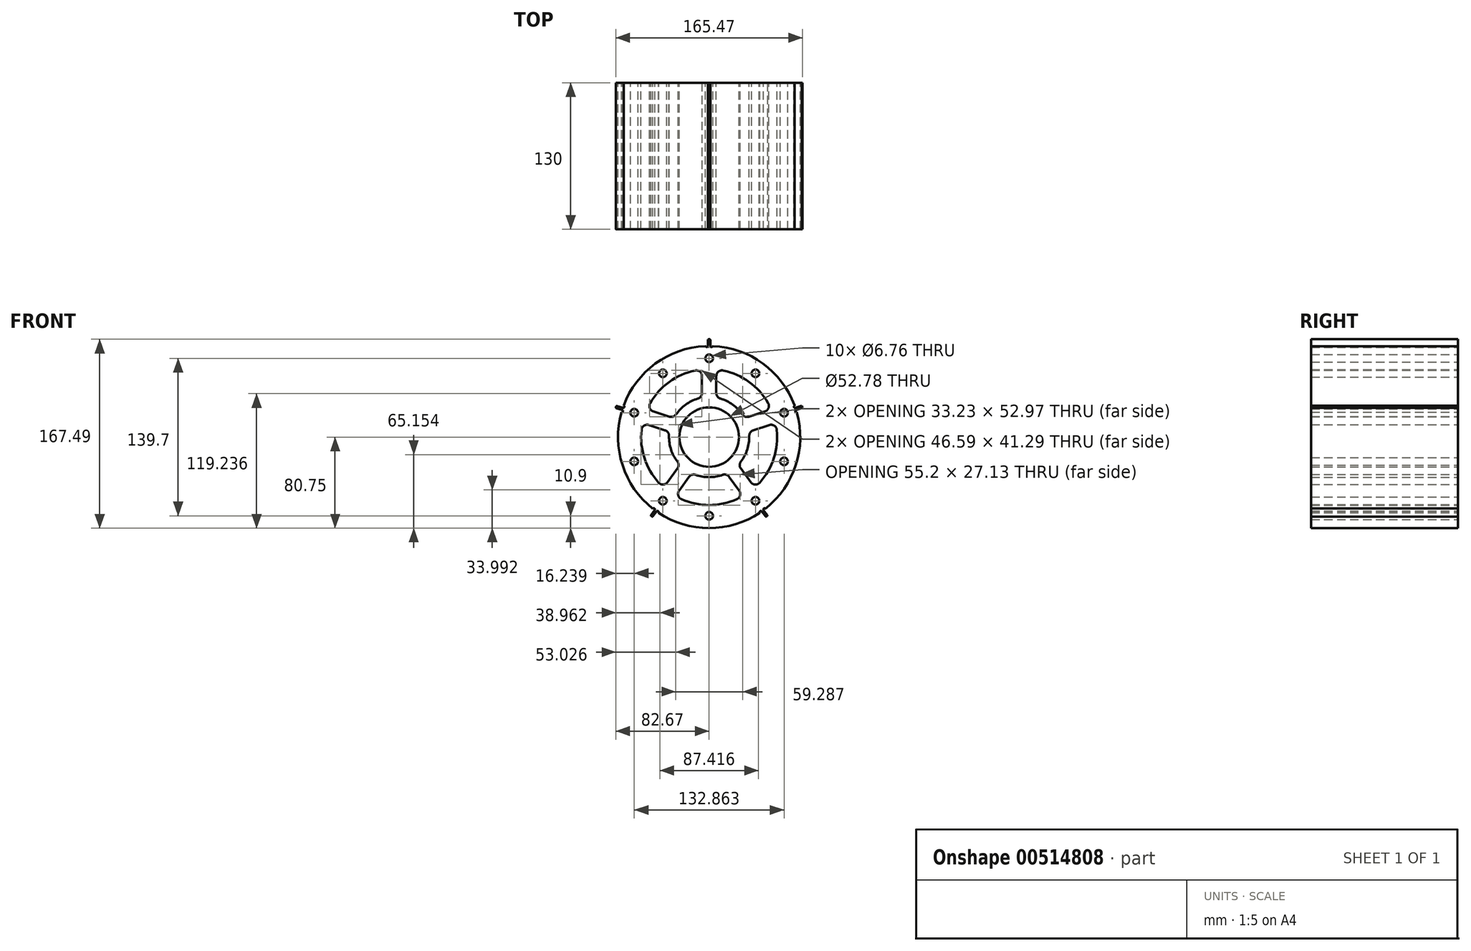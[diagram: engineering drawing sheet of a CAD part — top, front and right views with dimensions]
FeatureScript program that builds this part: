
annotation { "Feature Type Name" : "Feature", "Feature Type Description" : "" }
export const myFeature = defineFeature(function(context is Context, id is Id, definition is map)
    precondition{}
    {
        {
            var Q0;
            Q0=qCreatedBy(makeId("Front.planeOp"),FACE);
            var sketch = newSketch(context, id + "F0", { "sketchPlane" : qUnion([Q0])});
            skArc(sketch, "E0", {"start": v(-1, 80.74) * mm, "mid": v(-47.46, 65.33) * mm, "end": v(-76.48, 25.9) * mm});
            skLineSegment(sketch, "E1", {"start": v(0, 0) * mm, "end": v(0, 93.04) * mm, "construction": true});
            skLineSegment(sketch, "E2", {"start": v(-1, 86.74) * mm, "end": v(-1, 80.74) * mm});
            skLineSegment(sketch, "E3.MirrorCS", {"start": v(1, 86.74) * mm, "end": v(1, 80.74) * mm});
            skLineSegment(sketch, "E4", {"start": v(-1, 86.74) * mm, "end": v(1, 86.74) * mm});
            skLineSegment(sketch, "E5.1.0", {"start": v(-82.18, 27.75) * mm, "end": v(-76.48, 25.9) * mm});
            skLineSegment(sketch, "E5.1.1", {"start": v(-82.8, 25.85) * mm, "end": v(-82.18, 27.75) * mm});
            skLineSegment(sketch, "E5.1.2", {"start": v(-82.8, 25.85) * mm, "end": v(-77.1, 24) * mm});
            skLineSegment(sketch, "E5.2.0", {"start": v(-51.8, -69.58) * mm, "end": v(-48.27, -64.73) * mm});
            skLineSegment(sketch, "E5.2.1", {"start": v(-50.17, -70.76) * mm, "end": v(-51.8, -69.58) * mm});
            skLineSegment(sketch, "E5.2.2", {"start": v(-50.17, -70.76) * mm, "end": v(-46.65, -65.91) * mm});
            skLineSegment(sketch, "E5.3.0", {"start": v(50.17, -70.76) * mm, "end": v(46.65, -65.91) * mm});
            skLineSegment(sketch, "E5.3.1", {"start": v(51.8, -69.58) * mm, "end": v(50.17, -70.76) * mm});
            skLineSegment(sketch, "E5.3.2", {"start": v(51.8, -69.58) * mm, "end": v(48.27, -64.73) * mm});
            skArc(sketch, "E6.trimOffspring", {"start": v(-77.1, 24) * mm, "mid": v(-76.8, -24.95) * mm, "end": v(-48.27, -64.73) * mm});
            skArc(sketch, "E7.trimOffspring", {"start": v(76.48, 25.9) * mm, "mid": v(47.46, 65.33) * mm, "end": v(1, 80.74) * mm});
            skArc(sketch, "E8.trimOffspring", {"start": v(-46.65, -65.91) * mm, "mid": v(47.46, -65.33) * mm, "end": v(77.1, 24) * mm});
            skLineSegment(sketch, "E9.2.4.0", {"start": v(82.8, 25.85) * mm, "end": v(77.1, 24) * mm});
            skLineSegment(sketch, "E9.3.4.0", {"start": v(82.18, 27.75) * mm, "end": v(82.8, 25.85) * mm});
            skLineSegment(sketch, "E9.6.4.0", {"start": v(82.18, 27.75) * mm, "end": v(76.48, 25.9) * mm});
            skSolve(sketch);
        }
        {
            var Q0;
            Q0=qSketchRegion(id+"F0",true);
            extrude(context, id + "F1", {"entities" : qUnion([Q0]), "depth" : 130 * mm});
        }
        {
            var Q0;
            Q0=qCreatedBy(makeId("Front.planeOp"),FACE);
            var sketch = newSketch(context, id + "F2", { "sketchPlane" : qUnion([Q0])});
            skCircle(sketch, "E10", {"center": v(0, 0) * mm, "radius": 26.4 * mm});
            skSolve(sketch);
        }
        {
            var Q0;
            Q0=makeQuery(id+"F2.imprint","IMPRINT",FACE,{"disambiguationData":[TD([[makeQuery(id+"F2.imprint","IMPRINT",EDGE,{"derivedFrom":sQuery(id+"F2.wireOp",EDGE,"E10")}),1.0]])]});
            var Q1;
            Q1=makeQuery(id+"F1.opExtrude","CAP_FACE",FACE,{"disambiguationData":[OSD([sQuery(id+"F0.wireOp",EDGE,"E0"),sQuery(id+"F0.wireOp",EDGE,"E2"),sQuery(id+"F0.wireOp",EDGE,"E3.MirrorCS"),sQuery(id+"F0.wireOp",EDGE,"E4"),sQuery(id+"F0.wireOp",EDGE,"E5.1.0"),sQuery(id+"F0.wireOp",EDGE,"E5.1.1"),sQuery(id+"F0.wireOp",EDGE,"E5.1.2"),sQuery(id+"F0.wireOp",EDGE,"E5.2.0"),sQuery(id+"F0.wireOp",EDGE,"E5.2.1"),sQuery(id+"F0.wireOp",EDGE,"E5.2.2"),sQuery(id+"F0.wireOp",EDGE,"E5.3.0"),sQuery(id+"F0.wireOp",EDGE,"E5.3.1"),sQuery(id+"F0.wireOp",EDGE,"E5.3.2"),sQuery(id+"F0.wireOp",EDGE,"E6.trimOffspring"),sQuery(id+"F0.wireOp",EDGE,"E7.trimOffspring"),sQuery(id+"F0.wireOp",EDGE,"E8.trimOffspring")])],"isStart":false});
            extrude(context, id + "F3", {"entities" : qUnion([Q0]), "operationType" : NewBodyOperationType.REMOVE, "endBound" : BoundingType.UP_TO_SURFACE, "endBoundEntityFace" : qUnion([Q1]), "depth" : 25.4 * mm});
        }
        {
            var Q0;
            Q0=qCreatedBy(makeId("Front.planeOp"),FACE);
            var sketch = newSketch(context, id + "F4", { "sketchPlane" : qUnion([Q0])});
            skLineSegment(sketch, "E11", {"start": v(9.9, 57.53) * mm, "end": v(9.9, 40.92) * mm});
            skLineSegment(sketch, "E12", {"start": v(40.92, 9.9) * mm, "end": v(57.53, 9.9) * mm});
            skArc(sketch, "E13", {"start": v(66.9, 23.04) * mm, "mid": v(50.03, 50.03) * mm, "end": v(23.04, 66.9) * mm});
            skArc(sketch, "E14", {"start": v(32, 15.5) * mm, "mid": v(25.14, 25.14) * mm, "end": v(15.5, 32) * mm});
            skArc(sketch, "E15.filletArc", {"start": v(32, 15.5) * mm, "mid": v(35.66, 11.42) * mm, "end": v(40.92, 9.9) * mm});
            skArc(sketch, "E16.filletArc", {"start": v(9.9, 40.92) * mm, "mid": v(11.42, 35.66) * mm, "end": v(15.5, 32) * mm});
            skArc(sketch, "E17.filletArc", {"start": v(23.04, 66.9) * mm, "mid": v(14.06, 65.6) * mm, "end": v(9.9, 57.53) * mm});
            skArc(sketch, "E18.filletArc", {"start": v(57.53, 9.9) * mm, "mid": v(65.6, 14.06) * mm, "end": v(66.9, 23.04) * mm});
            skLineSegment(sketch, "E19", {"start": v(0, 0) * mm, "end": v(0, 68.56) * mm, "construction": true});
            skLineSegment(sketch, "E20", {"start": v(0, 0) * mm, "end": v(60.99, 0) * mm, "construction": true});
            skLineSegment(sketch, "E21.1.0", {"start": v(-57.53, 9.9) * mm, "end": v(-40.92, 9.9) * mm});
            skArc(sketch, "E21.1.1", {"start": v(-66.9, 23.04) * mm, "mid": v(-65.6, 14.06) * mm, "end": v(-57.53, 9.9) * mm});
            skArc(sketch, "E21.1.2", {"start": v(-23.04, 66.9) * mm, "mid": v(-50.03, 50.03) * mm, "end": v(-66.9, 23.04) * mm});
            skArc(sketch, "E21.1.3", {"start": v(-9.9, 57.53) * mm, "mid": v(-14.06, 65.6) * mm, "end": v(-23.04, 66.9) * mm});
            skLineSegment(sketch, "E21.1.4", {"start": v(-9.9, 40.92) * mm, "end": v(-9.9, 57.53) * mm});
            skArc(sketch, "E21.1.5", {"start": v(-15.5, 32) * mm, "mid": v(-11.42, 35.66) * mm, "end": v(-9.9, 40.92) * mm});
            skArc(sketch, "E21.1.6", {"start": v(-40.92, 9.9) * mm, "mid": v(-35.66, 11.42) * mm, "end": v(-32, 15.5) * mm});
            skArc(sketch, "E21.1.7", {"start": v(-15.5, 32) * mm, "mid": v(-25.14, 25.14) * mm, "end": v(-32, 15.5) * mm});
            skLineSegment(sketch, "E21.2.0", {"start": v(-9.9, -57.53) * mm, "end": v(-9.9, -40.92) * mm});
            skArc(sketch, "E21.2.1", {"start": v(-23.04, -66.9) * mm, "mid": v(-14.06, -65.6) * mm, "end": v(-9.9, -57.53) * mm});
            skArc(sketch, "E21.2.2", {"start": v(-66.9, -23.04) * mm, "mid": v(-50.03, -50.03) * mm, "end": v(-23.04, -66.9) * mm});
            skArc(sketch, "E21.2.3", {"start": v(-57.53, -9.9) * mm, "mid": v(-65.6, -14.06) * mm, "end": v(-66.9, -23.04) * mm});
            skLineSegment(sketch, "E21.2.4", {"start": v(-40.92, -9.9) * mm, "end": v(-57.53, -9.9) * mm});
            skArc(sketch, "E21.2.5", {"start": v(-32, -15.5) * mm, "mid": v(-35.66, -11.42) * mm, "end": v(-40.92, -9.9) * mm});
            skArc(sketch, "E21.2.6", {"start": v(-9.9, -40.92) * mm, "mid": v(-11.42, -35.66) * mm, "end": v(-15.5, -32) * mm});
            skArc(sketch, "E21.2.7", {"start": v(-32, -15.5) * mm, "mid": v(-25.14, -25.14) * mm, "end": v(-15.5, -32) * mm});
            skLineSegment(sketch, "E21.3.0", {"start": v(57.53, -9.9) * mm, "end": v(40.92, -9.9) * mm});
            skArc(sketch, "E21.3.1", {"start": v(66.9, -23.04) * mm, "mid": v(65.6, -14.06) * mm, "end": v(57.53, -9.9) * mm});
            skArc(sketch, "E21.3.2", {"start": v(23.04, -66.9) * mm, "mid": v(50.03, -50.03) * mm, "end": v(66.9, -23.04) * mm});
            skArc(sketch, "E21.3.3", {"start": v(9.9, -57.53) * mm, "mid": v(14.06, -65.6) * mm, "end": v(23.04, -66.9) * mm});
            skLineSegment(sketch, "E21.3.4", {"start": v(9.9, -40.92) * mm, "end": v(9.9, -57.53) * mm});
            skArc(sketch, "E21.3.5", {"start": v(15.5, -32) * mm, "mid": v(11.42, -35.66) * mm, "end": v(9.9, -40.92) * mm});
            skArc(sketch, "E21.3.6", {"start": v(40.92, -9.9) * mm, "mid": v(35.66, -11.42) * mm, "end": v(32, -15.5) * mm});
            skArc(sketch, "E21.3.7", {"start": v(15.5, -32) * mm, "mid": v(25.14, -25.14) * mm, "end": v(32, -15.5) * mm});
            skSolve(sketch);
        }
        {
            var Q0;
            Q0=makeQuery(id+"F1.opExtrude","CAP_FACE",FACE,{"disambiguationData":[OSD([sQuery(id+"F0.wireOp",EDGE,"E0"),sQuery(id+"F0.wireOp",EDGE,"E2"),sQuery(id+"F0.wireOp",EDGE,"E3.MirrorCS"),sQuery(id+"F0.wireOp",EDGE,"E4"),sQuery(id+"F0.wireOp",EDGE,"E5.1.0"),sQuery(id+"F0.wireOp",EDGE,"E5.1.1"),sQuery(id+"F0.wireOp",EDGE,"E5.1.2"),sQuery(id+"F0.wireOp",EDGE,"E5.2.0"),sQuery(id+"F0.wireOp",EDGE,"E5.2.1"),sQuery(id+"F0.wireOp",EDGE,"E5.2.2"),sQuery(id+"F0.wireOp",EDGE,"E5.3.0"),sQuery(id+"F0.wireOp",EDGE,"E5.3.1"),sQuery(id+"F0.wireOp",EDGE,"E5.3.2"),sQuery(id+"F0.wireOp",EDGE,"E6.trimOffspring"),sQuery(id+"F0.wireOp",EDGE,"E7.trimOffspring"),sQuery(id+"F0.wireOp",EDGE,"E8.trimOffspring")])],"isStart":true});
            var sketch = newSketch(context, id + "F5", { "sketchPlane" : qUnion([Q0])});
            skLineSegment(sketch, "E22", {"start": v(-1, 80.74) * mm, "end": v(-7.67, 80.74) * mm, "construction": true});
            skCircle(sketch, "E23", {"center": v(-2.02, 80.74) * mm, "radius": 1.02 * mm});
            skCircle(sketch, "E24.MirrorC", {"center": v(2.02, 80.74) * mm, "radius": 1.02 * mm});
            skCircle(sketch, "E25.1.0", {"center": v(-76.17, 26.87) * mm, "radius": 1.02 * mm});
            skCircle(sketch, "E25.1.1", {"center": v(-77.41, 23.03) * mm, "radius": 1.02 * mm});
            skCircle(sketch, "E25.2.0", {"center": v(-49.1, -64.14) * mm, "radius": 1.02 * mm});
            skCircle(sketch, "E25.2.1", {"center": v(-45.83, -66.5) * mm, "radius": 1.02 * mm});
            skCircle(sketch, "E25.3.0", {"center": v(45.83, -66.5) * mm, "radius": 1.02 * mm});
            skCircle(sketch, "E25.3.1", {"center": v(49.1, -64.14) * mm, "radius": 1.02 * mm});
            skPoint(sketch, "E25.center", {"position": v(0, 0) * mm});
            skCircle(sketch, "E26.1.4.0", {"center": v(77.41, 23.03) * mm, "radius": 1.02 * mm});
            skCircle(sketch, "E26.2.4.0", {"center": v(76.17, 26.87) * mm, "radius": 1.02 * mm});
            skSolve(sketch);
        }
        {
            var Q0;
            Q0=qSketchRegion(id+"F5",true);
            extrude(context, id + "F6", {"entities" : qUnion([Q0]), "operationType" : NewBodyOperationType.REMOVE, "endBound" : BoundingType.THROUGH_ALL, "oppositeDirection" : true, "depth" : 25.4 * mm});
        }
        {
            var Q0;
            Q0=makeQuery(id+"F1.opExtrude","SWEPT_EDGE",EDGE,{"disambiguationData":[OSD([sQuery(id+"F0.wireOp",EDGE,"E2"),sQuery(id+"F0.wireOp",EDGE,"E4")])]});
            var Q1;
            Q1=makeQuery(id+"F1.opExtrude","SWEPT_EDGE",EDGE,{"disambiguationData":[OSD([sQuery(id+"F0.wireOp",EDGE,"E3.MirrorCS"),sQuery(id+"F0.wireOp",EDGE,"E4")])]});
            var Q2;
            Q2=makeQuery(id+"F6.boolean.opBoolean","INTERSECT",EDGE,{"derivedFrom":[makeQuery(id+"F1.opExtrude","SWEPT_FACE",FACE,{"disambiguationData":[OSD([sQuery(id+"F0.wireOp",EDGE,"E0")])]}),makeQuery(id+"F6.opExtrude","SWEPT_FACE",FACE,{"disambiguationData":[OSD([sQuery(id+"F5.wireOp",EDGE,"E24.MirrorC")])]})]});
            var Q3;
            Q3=makeQuery(id+"F6.boolean.opBoolean","INTERSECT",EDGE,{"derivedFrom":[makeQuery(id+"F1.opExtrude","SWEPT_FACE",FACE,{"disambiguationData":[OSD([sQuery(id+"F0.wireOp",EDGE,"E7.trimOffspring")])]}),makeQuery(id+"F6.opExtrude","SWEPT_FACE",FACE,{"disambiguationData":[OSD([sQuery(id+"F5.wireOp",EDGE,"E23")])]})]});
            var Q4;
            Q4=makeQuery(id+"F6.boolean.opBoolean","INTERSECT",EDGE,{"derivedFrom":[makeQuery(id+"F1.opExtrude","SWEPT_FACE",FACE,{"disambiguationData":[OSD([sQuery(id+"F0.wireOp",EDGE,"E0")])]}),makeQuery(id+"F6.opExtrude","SWEPT_FACE",FACE,{"disambiguationData":[OSD([sQuery(id+"F5.wireOp",EDGE,"E25.3.1")])]})]});
            var Q5;
            Q5=makeQuery(id+"F1.opExtrude","SWEPT_EDGE",EDGE,{"disambiguationData":[OSD([sQuery(id+"F0.wireOp",EDGE,"E5.1.0"),sQuery(id+"F0.wireOp",EDGE,"E5.1.1")])]});
            var Q6;
            Q6=makeQuery(id+"F1.opExtrude","SWEPT_EDGE",EDGE,{"disambiguationData":[OSD([sQuery(id+"F0.wireOp",EDGE,"E5.1.1"),sQuery(id+"F0.wireOp",EDGE,"E5.1.2")])]});
            var Q7;
            Q7=makeQuery(id+"F6.boolean.opBoolean","INTERSECT",EDGE,{"derivedFrom":[makeQuery(id+"F1.opExtrude","SWEPT_FACE",FACE,{"disambiguationData":[OSD([sQuery(id+"F0.wireOp",EDGE,"E6.trimOffspring")])]}),makeQuery(id+"F6.opExtrude","SWEPT_FACE",FACE,{"disambiguationData":[OSD([sQuery(id+"F5.wireOp",EDGE,"E25.3.0")])]})]});
            var Q8;
            Q8=makeQuery(id+"F6.boolean.opBoolean","INTERSECT",EDGE,{"derivedFrom":[makeQuery(id+"F1.opExtrude","SWEPT_FACE",FACE,{"disambiguationData":[OSD([sQuery(id+"F0.wireOp",EDGE,"E6.trimOffspring")])]}),makeQuery(id+"F6.opExtrude","SWEPT_FACE",FACE,{"disambiguationData":[OSD([sQuery(id+"F5.wireOp",EDGE,"E25.2.1")])]})]});
            var Q9;
            Q9=makeQuery(id+"F1.opExtrude","SWEPT_EDGE",EDGE,{"disambiguationData":[OSD([sQuery(id+"F0.wireOp",EDGE,"E5.2.0"),sQuery(id+"F0.wireOp",EDGE,"E5.2.1")])]});
            var Q10;
            Q10=makeQuery(id+"F1.opExtrude","SWEPT_EDGE",EDGE,{"disambiguationData":[OSD([sQuery(id+"F0.wireOp",EDGE,"E5.2.1"),sQuery(id+"F0.wireOp",EDGE,"E5.2.2")])]});
            var Q11;
            Q11=makeQuery(id+"F6.boolean.opBoolean","INTERSECT",EDGE,{"derivedFrom":[makeQuery(id+"F1.opExtrude","SWEPT_FACE",FACE,{"disambiguationData":[OSD([sQuery(id+"F0.wireOp",EDGE,"E8.trimOffspring")])]}),makeQuery(id+"F6.opExtrude","SWEPT_FACE",FACE,{"disambiguationData":[OSD([sQuery(id+"F5.wireOp",EDGE,"E25.2.0")])]})]});
            var Q12;
            Q12=makeQuery(id+"F6.boolean.opBoolean","INTERSECT",EDGE,{"derivedFrom":[makeQuery(id+"F1.opExtrude","SWEPT_FACE",FACE,{"disambiguationData":[OSD([sQuery(id+"F0.wireOp",EDGE,"E8.trimOffspring")])]}),makeQuery(id+"F6.opExtrude","SWEPT_FACE",FACE,{"disambiguationData":[OSD([sQuery(id+"F5.wireOp",EDGE,"E25.1.1")])]})]});
            var Q13;
            Q13=makeQuery(id+"F1.opExtrude","SWEPT_EDGE",EDGE,{"disambiguationData":[OSD([sQuery(id+"F0.wireOp",EDGE,"E5.3.0"),sQuery(id+"F0.wireOp",EDGE,"E5.3.1")])]});
            var Q14;
            Q14=makeQuery(id+"F1.opExtrude","SWEPT_EDGE",EDGE,{"disambiguationData":[OSD([sQuery(id+"F0.wireOp",EDGE,"E5.3.1"),sQuery(id+"F0.wireOp",EDGE,"E5.3.2")])]});
            var Q15;
            Q15=makeQuery(id+"F6.boolean.opBoolean","INTERSECT",EDGE,{"derivedFrom":[makeQuery(id+"F1.opExtrude","SWEPT_FACE",FACE,{"disambiguationData":[OSD([sQuery(id+"F0.wireOp",EDGE,"E7.trimOffspring")])]}),makeQuery(id+"F6.opExtrude","SWEPT_FACE",FACE,{"disambiguationData":[OSD([sQuery(id+"F5.wireOp",EDGE,"E25.1.0")])]})]});
            fillet(context, id + "F7", {"entities" : qUnion([Q0, Q1, Q2, Q3, Q4, Q5, Q6, Q7, Q8, Q9, Q10, Q11, Q12, Q13, Q14, Q15]), "radius" : 0.5 * mm, "tangentPropagation" : true, "allowEdgeOverflow" : false});
        }
        {
            var Q0;
            Q0=makeQuery(id+"F1.opExtrude","CAP_FACE",FACE,{"disambiguationData":[OSD([sQuery(id+"F0.wireOp",EDGE,"E0"),sQuery(id+"F0.wireOp",EDGE,"E2"),sQuery(id+"F0.wireOp",EDGE,"E3.MirrorCS"),sQuery(id+"F0.wireOp",EDGE,"E4"),sQuery(id+"F0.wireOp",EDGE,"E5.1.0"),sQuery(id+"F0.wireOp",EDGE,"E5.1.1"),sQuery(id+"F0.wireOp",EDGE,"E5.1.2"),sQuery(id+"F0.wireOp",EDGE,"E5.2.0"),sQuery(id+"F0.wireOp",EDGE,"E5.2.1"),sQuery(id+"F0.wireOp",EDGE,"E5.2.2"),sQuery(id+"F0.wireOp",EDGE,"E5.3.0"),sQuery(id+"F0.wireOp",EDGE,"E5.3.1"),sQuery(id+"F0.wireOp",EDGE,"E5.3.2"),sQuery(id+"F0.wireOp",EDGE,"E6.trimOffspring"),sQuery(id+"F0.wireOp",EDGE,"E7.trimOffspring"),sQuery(id+"F0.wireOp",EDGE,"E8.trimOffspring"),sQuery(id+"F0.wireOp",EDGE,"E9.2.4.0"),sQuery(id+"F0.wireOp",EDGE,"E9.3.4.0"),sQuery(id+"F0.wireOp",EDGE,"E9.6.4.0")])],"isStart":true});
            var sketch = newSketch(context, id + "F8", { "sketchPlane" : qUnion([Q0])});
            skArc(sketch, "E27", {"start": v(-6.35, 59.99) * mm, "mid": v(-35.46, 48.8) * mm, "end": v(-55.1, 24.58) * mm});
            skArc(sketch, "E28", {"start": v(-6.35, 34.99) * mm, "mid": v(-20.9, 28.77) * mm, "end": v(-31.31, 16.85) * mm});
            skLineSegment(sketch, "E29", {"start": v(-6.35, 59.99) * mm, "end": v(-6.35, 34.99) * mm});
            skLineSegment(sketch, "E30", {"start": v(6.35, 59.99) * mm, "end": v(6.35, 34.99) * mm});
            skLineSegment(sketch, "E31.1.0", {"start": v(-59.02, 12.5) * mm, "end": v(-35.24, 4.77) * mm});
            skLineSegment(sketch, "E31.1.1", {"start": v(-55.1, 24.58) * mm, "end": v(-31.31, 16.85) * mm});
            skLineSegment(sketch, "E31.2.0", {"start": v(-30.12, -52.27) * mm, "end": v(-15.43, -32.04) * mm});
            skLineSegment(sketch, "E31.2.1", {"start": v(-40.4, -44.8) * mm, "end": v(-25.7, -24.57) * mm});
            skLineSegment(sketch, "E31.3.0", {"start": v(40.4, -44.8) * mm, "end": v(25.7, -24.57) * mm});
            skLineSegment(sketch, "E31.3.1", {"start": v(30.12, -52.27) * mm, "end": v(15.43, -32.04) * mm});
            skLineSegment(sketch, "E31.4.0", {"start": v(55.1, 24.58) * mm, "end": v(31.31, 16.85) * mm});
            skLineSegment(sketch, "E31.4.1", {"start": v(59.02, 12.5) * mm, "end": v(35.24, 4.77) * mm});
            skArc(sketch, "E32.trimOffspring", {"start": v(-59.02, 12.5) * mm, "mid": v(-57.37, -18.64) * mm, "end": v(-40.4, -44.8) * mm});
            skArc(sketch, "E33.trimOffspring", {"start": v(-35.24, 4.77) * mm, "mid": v(-33.82, -10.99) * mm, "end": v(-25.7, -24.57) * mm});
            skArc(sketch, "E34.trimOffspring", {"start": v(-15.43, -32.04) * mm, "mid": v(0, -35.56) * mm, "end": v(15.43, -32.04) * mm});
            skArc(sketch, "E35.trimOffspring", {"start": v(-30.12, -52.27) * mm, "mid": v(0, -60.33) * mm, "end": v(30.12, -52.27) * mm});
            skArc(sketch, "E36.trimOffspring", {"start": v(40.4, -44.8) * mm, "mid": v(57.37, -18.64) * mm, "end": v(59.02, 12.5) * mm});
            skArc(sketch, "E37.trimOffspring", {"start": v(25.7, -24.57) * mm, "mid": v(33.82, -10.99) * mm, "end": v(35.24, 4.77) * mm});
            skArc(sketch, "E38.trimOffspring", {"start": v(31.31, 16.85) * mm, "mid": v(20.9, 28.77) * mm, "end": v(6.35, 34.99) * mm});
            skArc(sketch, "E39.trimOffspring", {"start": v(55.1, 24.58) * mm, "mid": v(35.46, 48.8) * mm, "end": v(6.35, 59.99) * mm});
            skSolve(sketch);
        }
        {
            var Q0;
            Q0=makeQuery(id+"F8.imprint","IMPRINT",FACE,{"disambiguationData":[TD([[makeQuery(id+"F8.imprint","IMPRINT",EDGE,{"derivedFrom":sQuery(id+"F8.wireOp",EDGE,"E27")}),1.0]])]});
            var Q1;
            Q1=makeQuery(id+"F8.imprint","IMPRINT",FACE,{"disambiguationData":[TD([[makeQuery(id+"F8.imprint","IMPRINT",EDGE,{"derivedFrom":sQuery(id+"F8.wireOp",EDGE,"E30")}),1.0]])]});
            var Q2;
            Q2=makeQuery(id+"F8.imprint","IMPRINT",FACE,{"disambiguationData":[TD([[makeQuery(id+"F8.imprint","IMPRINT",EDGE,{"derivedFrom":sQuery(id+"F8.wireOp",EDGE,"E31.3.0")}),-1.0]])]});
            var Q3;
            Q3=makeQuery(id+"F8.imprint","IMPRINT",FACE,{"disambiguationData":[TD([[makeQuery(id+"F8.imprint","IMPRINT",EDGE,{"derivedFrom":sQuery(id+"F8.wireOp",EDGE,"E31.2.0")}),-1.0]])]});
            var Q4;
            Q4=makeQuery(id+"F8.imprint","IMPRINT",FACE,{"disambiguationData":[TD([[makeQuery(id+"F8.imprint","IMPRINT",EDGE,{"derivedFrom":sQuery(id+"F8.wireOp",EDGE,"E31.1.0")}),-1.0]])]});
            extrude(context, id + "F9", {"entities" : qUnion([Q0, Q1, Q2, Q3, Q4]), "operationType" : NewBodyOperationType.REMOVE, "endBound" : BoundingType.THROUGH_ALL, "oppositeDirection" : true, "depth" : 25.4 * mm});
        }
        {
            var Q0;
            Q0=makeQuery(id+"F9.boolean.opBoolean","COPY",EDGE,{"derivedFrom":makeQuery(id+"F9.opExtrude","SWEPT_EDGE",EDGE,{"disambiguationData":[OSD([sQuery(id+"F8.wireOp",EDGE,"E27"),sQuery(id+"F8.wireOp",EDGE,"E31.1.1")])]})});
            var Q1;
            Q1=makeQuery(id+"F9.boolean.opBoolean","COPY",EDGE,{"derivedFrom":makeQuery(id+"F9.opExtrude","SWEPT_EDGE",EDGE,{"disambiguationData":[OSD([sQuery(id+"F8.wireOp",EDGE,"E28"),sQuery(id+"F8.wireOp",EDGE,"E31.1.1")])]})});
            var Q2;
            Q2=makeQuery(id+"F9.boolean.opBoolean","COPY",EDGE,{"derivedFrom":makeQuery(id+"F9.opExtrude","SWEPT_EDGE",EDGE,{"disambiguationData":[OSD([sQuery(id+"F8.wireOp",EDGE,"E28"),sQuery(id+"F8.wireOp",EDGE,"E29")])]})});
            var Q3;
            Q3=makeQuery(id+"F9.boolean.opBoolean","COPY",EDGE,{"derivedFrom":makeQuery(id+"F9.opExtrude","SWEPT_EDGE",EDGE,{"disambiguationData":[OSD([sQuery(id+"F8.wireOp",EDGE,"E27"),sQuery(id+"F8.wireOp",EDGE,"E29")])]})});
            var Q4;
            Q4=makeQuery(id+"F9.boolean.opBoolean","COPY",EDGE,{"derivedFrom":makeQuery(id+"F9.opExtrude","SWEPT_EDGE",EDGE,{"disambiguationData":[OSD([sQuery(id+"F8.wireOp",EDGE,"E31.4.0"),sQuery(id+"F8.wireOp",EDGE,"E39.trimOffspring")])]})});
            var Q5;
            Q5=makeQuery(id+"F9.boolean.opBoolean","COPY",EDGE,{"derivedFrom":makeQuery(id+"F9.opExtrude","SWEPT_EDGE",EDGE,{"disambiguationData":[OSD([sQuery(id+"F8.wireOp",EDGE,"E31.4.0"),sQuery(id+"F8.wireOp",EDGE,"E38.trimOffspring")])]})});
            var Q6;
            Q6=makeQuery(id+"F9.boolean.opBoolean","COPY",EDGE,{"derivedFrom":makeQuery(id+"F9.opExtrude","SWEPT_EDGE",EDGE,{"disambiguationData":[OSD([sQuery(id+"F8.wireOp",EDGE,"E30"),sQuery(id+"F8.wireOp",EDGE,"E38.trimOffspring")])]})});
            var Q7;
            Q7=makeQuery(id+"F9.boolean.opBoolean","COPY",EDGE,{"derivedFrom":makeQuery(id+"F9.opExtrude","SWEPT_EDGE",EDGE,{"disambiguationData":[OSD([sQuery(id+"F8.wireOp",EDGE,"E30"),sQuery(id+"F8.wireOp",EDGE,"E39.trimOffspring")])]})});
            var Q8;
            Q8=makeQuery(id+"F9.boolean.opBoolean","COPY",EDGE,{"derivedFrom":makeQuery(id+"F9.opExtrude","SWEPT_EDGE",EDGE,{"disambiguationData":[OSD([sQuery(id+"F8.wireOp",EDGE,"E31.4.1"),sQuery(id+"F8.wireOp",EDGE,"E36.trimOffspring")])]})});
            var Q9;
            Q9=makeQuery(id+"F9.boolean.opBoolean","COPY",EDGE,{"derivedFrom":makeQuery(id+"F9.opExtrude","SWEPT_EDGE",EDGE,{"disambiguationData":[OSD([sQuery(id+"F8.wireOp",EDGE,"E31.3.0"),sQuery(id+"F8.wireOp",EDGE,"E36.trimOffspring")])]})});
            var Q10;
            Q10=makeQuery(id+"F9.boolean.opBoolean","COPY",EDGE,{"derivedFrom":makeQuery(id+"F9.opExtrude","SWEPT_EDGE",EDGE,{"disambiguationData":[OSD([sQuery(id+"F8.wireOp",EDGE,"E31.3.0"),sQuery(id+"F8.wireOp",EDGE,"E37.trimOffspring")])]})});
            var Q11;
            Q11=makeQuery(id+"F9.boolean.opBoolean","COPY",EDGE,{"derivedFrom":makeQuery(id+"F9.opExtrude","SWEPT_EDGE",EDGE,{"disambiguationData":[OSD([sQuery(id+"F8.wireOp",EDGE,"E31.4.1"),sQuery(id+"F8.wireOp",EDGE,"E37.trimOffspring")])]})});
            var Q12;
            Q12=makeQuery(id+"F9.boolean.opBoolean","COPY",EDGE,{"derivedFrom":makeQuery(id+"F9.opExtrude","SWEPT_EDGE",EDGE,{"disambiguationData":[OSD([sQuery(id+"F8.wireOp",EDGE,"E31.2.0"),sQuery(id+"F8.wireOp",EDGE,"E35.trimOffspring")])]})});
            var Q13;
            Q13=makeQuery(id+"F9.boolean.opBoolean","COPY",EDGE,{"derivedFrom":makeQuery(id+"F9.opExtrude","SWEPT_EDGE",EDGE,{"disambiguationData":[OSD([sQuery(id+"F8.wireOp",EDGE,"E31.3.1"),sQuery(id+"F8.wireOp",EDGE,"E35.trimOffspring")])]})});
            var Q14;
            Q14=makeQuery(id+"F9.boolean.opBoolean","COPY",EDGE,{"derivedFrom":makeQuery(id+"F9.opExtrude","SWEPT_EDGE",EDGE,{"disambiguationData":[OSD([sQuery(id+"F8.wireOp",EDGE,"E31.3.1"),sQuery(id+"F8.wireOp",EDGE,"E34.trimOffspring")])]})});
            var Q15;
            Q15=makeQuery(id+"F9.boolean.opBoolean","COPY",EDGE,{"derivedFrom":makeQuery(id+"F9.opExtrude","SWEPT_EDGE",EDGE,{"disambiguationData":[OSD([sQuery(id+"F8.wireOp",EDGE,"E31.2.0"),sQuery(id+"F8.wireOp",EDGE,"E34.trimOffspring")])]})});
            var Q16;
            Q16=makeQuery(id+"F9.boolean.opBoolean","COPY",EDGE,{"derivedFrom":makeQuery(id+"F9.opExtrude","SWEPT_EDGE",EDGE,{"disambiguationData":[OSD([sQuery(id+"F8.wireOp",EDGE,"E31.1.0"),sQuery(id+"F8.wireOp",EDGE,"E33.trimOffspring")])]})});
            var Q17;
            Q17=makeQuery(id+"F9.boolean.opBoolean","COPY",EDGE,{"derivedFrom":makeQuery(id+"F9.opExtrude","SWEPT_EDGE",EDGE,{"disambiguationData":[OSD([sQuery(id+"F8.wireOp",EDGE,"E31.2.1"),sQuery(id+"F8.wireOp",EDGE,"E33.trimOffspring")])]})});
            var Q18;
            Q18=makeQuery(id+"F9.boolean.opBoolean","COPY",EDGE,{"derivedFrom":makeQuery(id+"F9.opExtrude","SWEPT_EDGE",EDGE,{"disambiguationData":[OSD([sQuery(id+"F8.wireOp",EDGE,"E31.2.1"),sQuery(id+"F8.wireOp",EDGE,"E32.trimOffspring")])]})});
            var Q19;
            Q19=makeQuery(id+"F9.boolean.opBoolean","COPY",EDGE,{"derivedFrom":makeQuery(id+"F9.opExtrude","SWEPT_EDGE",EDGE,{"disambiguationData":[OSD([sQuery(id+"F8.wireOp",EDGE,"E31.1.0"),sQuery(id+"F8.wireOp",EDGE,"E32.trimOffspring")])]})});
            fillet(context, id + "F10", {"entities" : qUnion([Q0, Q1, Q2, Q3, Q4, Q5, Q6, Q7, Q8, Q9, Q10, Q11, Q12, Q13, Q14, Q15, Q16, Q17, Q18, Q19]), "radius" : 5.08 * mm, "tangentPropagation" : true, "allowEdgeOverflow" : false});
        }
        {
            var Q0;
            Q0=makeQuery(id+"F1.opExtrude","CAP_FACE",FACE,{"disambiguationData":[OSD([sQuery(id+"F0.wireOp",EDGE,"E0"),sQuery(id+"F0.wireOp",EDGE,"E2"),sQuery(id+"F0.wireOp",EDGE,"E3.MirrorCS"),sQuery(id+"F0.wireOp",EDGE,"E4"),sQuery(id+"F0.wireOp",EDGE,"E5.1.0"),sQuery(id+"F0.wireOp",EDGE,"E5.1.1"),sQuery(id+"F0.wireOp",EDGE,"E5.1.2"),sQuery(id+"F0.wireOp",EDGE,"E5.2.0"),sQuery(id+"F0.wireOp",EDGE,"E5.2.1"),sQuery(id+"F0.wireOp",EDGE,"E5.2.2"),sQuery(id+"F0.wireOp",EDGE,"E5.3.0"),sQuery(id+"F0.wireOp",EDGE,"E5.3.1"),sQuery(id+"F0.wireOp",EDGE,"E5.3.2"),sQuery(id+"F0.wireOp",EDGE,"E6.trimOffspring"),sQuery(id+"F0.wireOp",EDGE,"E7.trimOffspring"),sQuery(id+"F0.wireOp",EDGE,"E8.trimOffspring"),sQuery(id+"F0.wireOp",EDGE,"E9.2.4.0"),sQuery(id+"F0.wireOp",EDGE,"E9.3.4.0"),sQuery(id+"F0.wireOp",EDGE,"E9.6.4.0")])],"isStart":true});
            var sketch = newSketch(context, id + "F11", { "sketchPlane" : qUnion([Q0])});
            skCircle(sketch, "E40", {"center": v(0, 0) * mm, "radius": 69.85 * mm, "construction": true});
            skLineSegment(sketch, "E41", {"start": v(0, 85.6) * mm, "end": v(0, 68.09) * mm, "construction": true});
            skPoint(sketch, "E41.startSnap0", {"position": v(0, 86.74) * mm});
            skPoint(sketch, "E42", {"position": v(0, 69.85) * mm});
            skPoint(sketch, "E43.1.0", {"position": v(-41.06, 56.5) * mm});
            skPoint(sketch, "E43.2.0", {"position": v(-66.43, 21.58) * mm});
            skPoint(sketch, "E43.3.0", {"position": v(-66.43, -21.58) * mm});
            skPoint(sketch, "E43.4.0", {"position": v(-41.06, -56.5) * mm});
            skPoint(sketch, "E43.5.0", {"position": v(0, -69.85) * mm});
            skPoint(sketch, "E43.6.0", {"position": v(41.06, -56.5) * mm});
            skPoint(sketch, "E43.7.0", {"position": v(66.43, -21.58) * mm});
            skPoint(sketch, "E44.0.8.0", {"position": v(66.43, 21.58) * mm});
            skPoint(sketch, "E44.0.9.0", {"position": v(41.06, 56.5) * mm});
            skSolve(sketch);
        }
        {
            var Q0;
            Q0=sQuery(id+"F11.wireOp",VERTEX,"E42");
            var Q1;
            Q1=sQuery(id+"F11.wireOp",VERTEX,"E43.1.0");
            var Q2;
            Q2=sQuery(id+"F11.wireOp",VERTEX,"E43.2.0");
            var Q3;
            Q3=sQuery(id+"F11.wireOp",VERTEX,"E43.3.0");
            var Q4;
            Q4=sQuery(id+"F11.wireOp",VERTEX,"E43.4.0");
            var Q5;
            Q5=sQuery(id+"F11.wireOp",VERTEX,"E43.5.0");
            var Q6;
            Q6=sQuery(id+"F11.wireOp",VERTEX,"E43.6.0");
            var Q7;
            Q7=sQuery(id+"F11.wireOp",VERTEX,"E43.7.0");
            var Q8;
            Q8=sQuery(id+"F11.wireOp",VERTEX,"E44.0.8.0");
            var Q9;
            Q9=sQuery(id+"F11.wireOp",VERTEX,"E44.0.9.0");
            var Q10;
            Q10=makeQuery(id+"F1.opExtrude","SWEPT_BODY",BODY,{"disambiguationData":[OSD([sQuery(id+"F0.wireOp",EDGE,"E0"),sQuery(id+"F0.wireOp",EDGE,"E2"),sQuery(id+"F0.wireOp",EDGE,"E3.MirrorCS"),sQuery(id+"F0.wireOp",EDGE,"E4"),sQuery(id+"F0.wireOp",EDGE,"E5.1.0"),sQuery(id+"F0.wireOp",EDGE,"E5.1.1"),sQuery(id+"F0.wireOp",EDGE,"E5.1.2"),sQuery(id+"F0.wireOp",EDGE,"E5.2.0"),sQuery(id+"F0.wireOp",EDGE,"E5.2.1"),sQuery(id+"F0.wireOp",EDGE,"E5.2.2"),sQuery(id+"F0.wireOp",EDGE,"E5.3.0"),sQuery(id+"F0.wireOp",EDGE,"E5.3.1"),sQuery(id+"F0.wireOp",EDGE,"E5.3.2"),sQuery(id+"F0.wireOp",EDGE,"E6.trimOffspring"),sQuery(id+"F0.wireOp",EDGE,"E7.trimOffspring"),sQuery(id+"F0.wireOp",EDGE,"E8.trimOffspring"),sQuery(id+"F0.wireOp",EDGE,"E9.2.4.0"),sQuery(id+"F0.wireOp",EDGE,"E9.3.4.0"),sQuery(id+"F0.wireOp",EDGE,"E9.6.4.0")])]});
            hole(context, id + "F12", {"style" : HoleStyle.SIMPLE, "endStyle" : HoleEndStyle.THROUGH, "standardTappedOrClearance" : lookupTablePath({ "standard" : "ANSI", "fit" : "Normal (ASME)", "size" : "1/4", "type" : "Clearance" }), "standardBlindInLast" : lookupTablePath({ "fit" : "Free", "standard" : "ANSI", "size" : "1/4", "type" : "Clearance" }), "holeDiameter" : 6.76 * mm, "tappedDepth" : 25.4 * mm, "tapClearance" : 3, "startFromSketch" : true, "locations" : qUnion([Q0, Q1, Q2, Q3, Q4, Q5, Q6, Q7, Q8, Q9]), "scope" : qUnion([Q10])});
        }
    });
